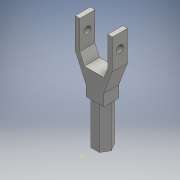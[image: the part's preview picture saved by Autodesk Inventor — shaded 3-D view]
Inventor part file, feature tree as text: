
AUTODESK INVENTOR PART (.ipt)
format: ipt  version: 2016 (Build 200138000, 138)  size: 148,480 bytes
history: native  units: mm
features: sketch x5, extrude x4
ambient origin geometry x8: Origin, YZ Plane, XZ Plane, XY Plane, X Axis, Y Axis, Z Axis, Center Point
bodies: Solid1 (feature_tree)
feature tree (9):
  extrude  "Extrusion1"  Depth=18.0mm TaperAngle=0.0deg
  extrude  "Extrusion2"  Depth=2.0mm
  sketch  "Sketch3"  dims[d16=27.824719mm d17=11.0mm]
  extrude  "Extrusion3"  Depth=11.0mm
  extrude  "Extrusion4"  Depth=6.5mm TaperAngle=0.0deg
  sketch  "Sketch1"  dims[d0=7.5mm d1=18.0mm d2=0.0mm]
  sketch  "Sketch2"  dims[d12=2.0mm d13=2.0mm]
  sketch  "Sketch5"  dims[d21=12.0mm d22=6.5mm d23=0.0mm]
  sketch  "Sketch6"  dims[d25=6.5mm d26=0.0mm d27=6.0mm d28=3.0mm d29=6.5mm d30=0.0mm d31=2.0mm d32=2.0mm]
